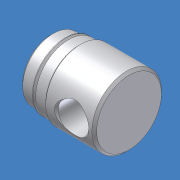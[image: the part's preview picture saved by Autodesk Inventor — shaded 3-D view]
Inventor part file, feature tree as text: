
AUTODESK INVENTOR PART (.ipt)
format: ipt  version: 2012 (Build 160160000, 160)  size: 197,120 bytes
history: native  units: mm (DEFAULTED — no unit token found)
features: other x85, revolve x4, sketch x4
ambient origin geometry x8: Origin, YZ Plane, XZ Plane, XY Plane, X Axis, Y Axis, Z Axis, Center Point
bodies: Solid1 (feature_tree)
feature tree (93):
  other  "04PQ0000_rear_head"
  revolve  "Revolution1"  Angle=360.0deg
  revolve  "Revolution2"  Angle=360.0deg
  revolve  "Revolution3"  [1 undecoded]
  revolve  "Revolution4"  [1 undecoded]
  other  "to_tube_XY"
  other  "to_tube_YZ"
  other  "to_tube_ZX"
  other  "to_tube_X"
  other  "to_tube_Y"
  other  "to_tube_Z"
  other  "to_tube_Center"
  other  "to_nut_XY"
  other  "to_nut_YZ"
  other  "to_nut_ZX"
  other  "to_nut_X"
  other  "to_nut_Y"
  other  "to_nut_Z"
  other  "to_nut_Center"
  other  "lovra1_XY"
  other  "lovra1_YZ"
  other  "lovra1_ZX"
  other  "lovra1_X"
  other  "lovra1_Y"
  other  "lovra1_Z"
  other  "lovra1_Center"
  other  "lovra2_XY"
  other  "lovra2_YZ"
  other  "lovra2_ZX"
  other  "lovra2_X"
  other  "lovra2_Y"
  other  "lovra2_Z"
  other  "lovra2_Center"
  other  "lovra3_XY"
  other  "lovra3_YZ"
  other  "lovra3_ZX"
  other  "lovra3_X"
  other  "lovra3_Y"
  other  "lovra3_Z"
  other  "lovra3_Center"
  other  "olen_XY"
  other  "olen_YZ"
  other  "olen_ZX"
  other  "olen_X"
  other  "olen_Y"
  other  "olen_Z"
  other  "olen_Center"
  other  "port2_XY"
  other  "port2_YZ"
  other  "port2_ZX"
  other  "port2_X"
  other  "port2_Y"
  other  "port2_Z"
  other  "port2_Center"
  other  "port_XY"
  other  "port_YZ"
  other  "port_ZX"
  other  "port_X"
  other  "port_Y"
  other  "port_Z"
  other  "port_Center"
  other  "lovra21_XY"
  other  "lovra21_YZ"
  other  "lovra21_ZX"
  other  "lovra21_X"
  other  "lovra21_Y"
  other  "lovra21_Z"
  other  "lovra21_Center"
  other  "lovra22_XY"
  other  "lovra22_YZ"
  other  "lovra22_ZX"
  other  "lovra22_X"
  other  "lovra22_Y"
  other  "lovra22_Z"
  other  "lovra22_Center"
  other  "to_screw_XY"
  other  "to_screw_YZ"
  other  "to_screw_ZX"
  other  "to_screw_X"
  other  "to_screw_Y"
  other  "to_screw_Z"
  other  "to_screw_Center"
  other  "to_mounting_bracket_XY"
  other  "to_mounting_bracket_YZ"
  other  "to_mounting_bracket_ZX"
  other  "to_mounting_bracket_X"
  other  "to_mounting_bracket_Y"
  other  "to_mounting_bracket_Z"
  other  "to_mounting_bracket_Center"
  sketch  "Sketch_8"  dims[d0=360.0deg d1=360.0deg]
  sketch  "Sketch_13"  dims[d2=360.0deg d3=360.0deg]
  sketch  "Sketch_19"
  sketch  "Sketch_24"
note: 2 required parameter values undecoded (feature->parameter linkage not recoverable at this tier; creation-order binding heuristic only, values carry confidence <= 0.55)
